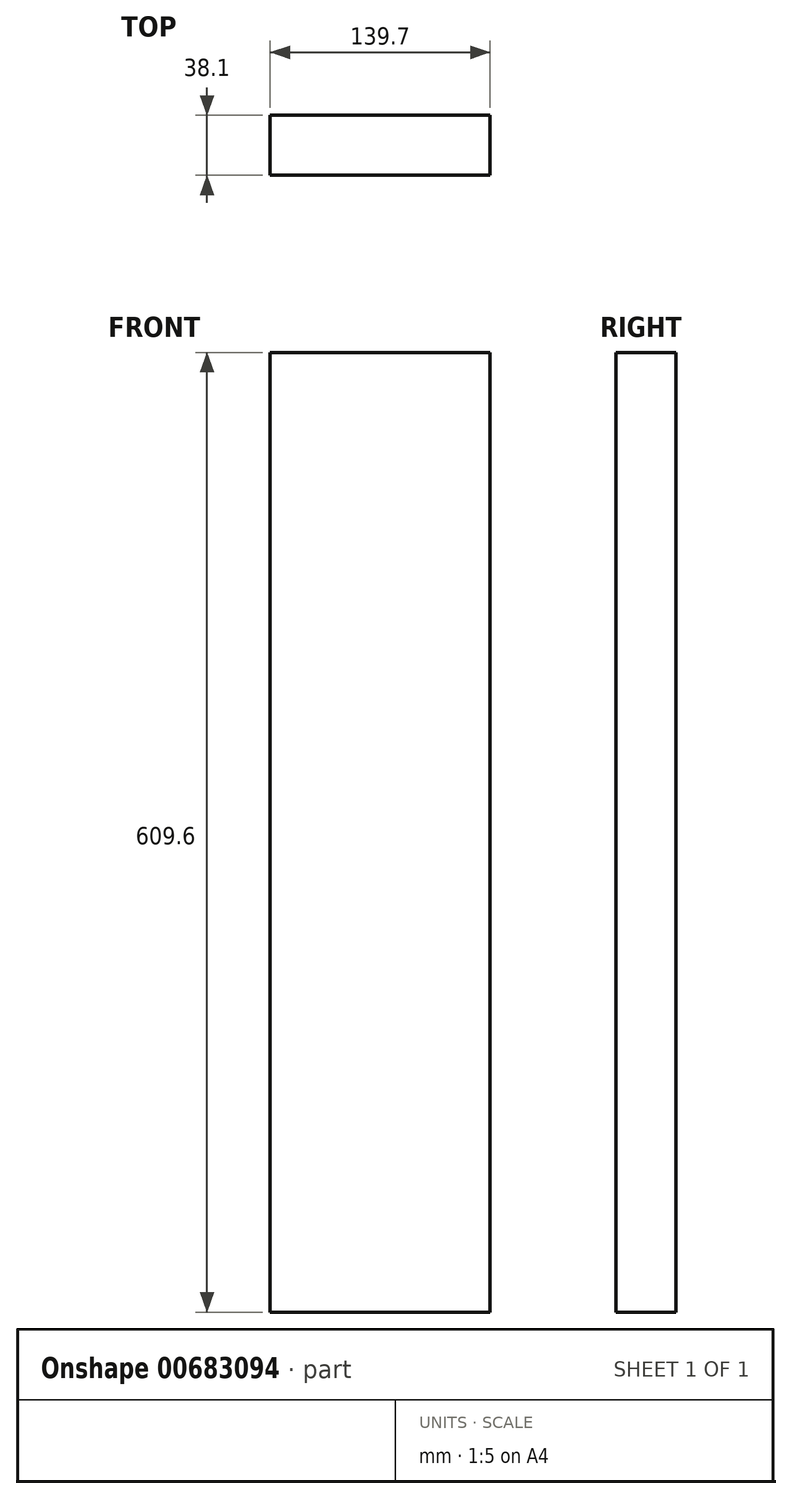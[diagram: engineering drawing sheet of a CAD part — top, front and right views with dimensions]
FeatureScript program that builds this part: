
annotation { "Feature Type Name" : "Feature", "Feature Type Description" : "" }
export const myFeature = defineFeature(function(context is Context, id is Id, definition is map)
    precondition{}
    {
        {
            var Q0;
            Q0=qCreatedBy(makeId("Top.planeOp"),FACE);
            var sketch = newSketch(context, id + "F0", { "sketchPlane" : qUnion([Q0])});
            skLineSegment(sketch, "E0.bottom", {"start": v(69.85, 19.05) * mm, "end": v(-69.85, 19.05) * mm});
            skLineSegment(sketch, "E0.top", {"start": v(69.85, -19.05) * mm, "end": v(-69.85, -19.05) * mm});
            skLineSegment(sketch, "E0.left", {"start": v(69.85, 19.05) * mm, "end": v(69.85, -19.05) * mm});
            skLineSegment(sketch, "E0.right", {"start": v(-69.85, 19.05) * mm, "end": v(-69.85, -19.05) * mm});
            skPoint(sketch, "E0.middle", {"position": v(0, 0) * mm});
            skSolve(sketch);
        }
        {
            var Q0;
            Q0 = qSketchRegion(id + "F0", true);
            extrude(context, id + "F1", {"entities" : qUnion([Q0]), "depth" : 609.6 * mm, "offsetDistance" : 25.4 * mm});
        }
    });
